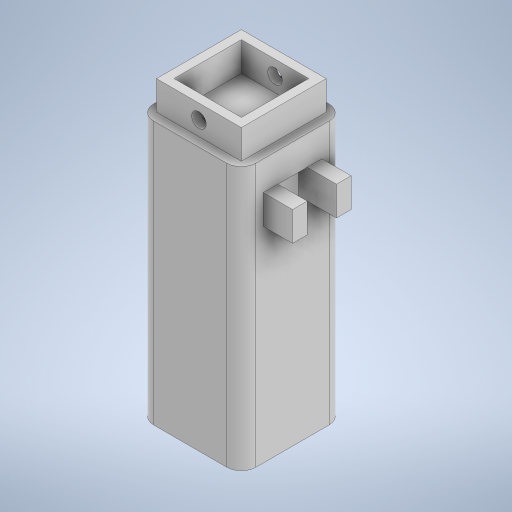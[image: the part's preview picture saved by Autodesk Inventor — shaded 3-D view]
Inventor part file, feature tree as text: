
AUTODESK INVENTOR PART (.ipt)
format: ipt  version: 2023 (Build 270158000, 158)  size: 302,592 bytes
history: native  units: mm
features: extrude x7, sketch x3, fillet x1
ambient origin geometry x8: Origin, YZ Plane, XZ Plane, XY Plane, X Axis, Y Axis, Z Axis, Center Point
bodies: Solido1 (feature_tree)
feature tree (11):
  sketch  "Schizzo2"
  extrude  "Estrusione1"  Depth=23.0mm
  extrude  "Estrusione2"  Depth=35.0mm
  extrude  "Estrusione3"  Depth=3.0mm
  fillet  "Raccordo1"  Radius=10.0mm
  extrude  "Estrusione4"  Depth=90.0mm TaperAngle=0.0deg
  sketch  "Schizzo4"
  extrude  "Estrusione5"  Depth=5.0mm TaperAngle=0.0deg
  extrude  "Estrusione6"  Depth=5.0mm
  extrude  "Estrusione7"  Depth=5.0mm
  sketch  "Schizzo3"
